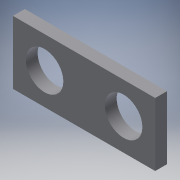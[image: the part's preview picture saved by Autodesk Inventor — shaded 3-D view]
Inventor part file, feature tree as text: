
AUTODESK INVENTOR PART (.ipt)
format: ipt  version: 2016 (Build 200138000, 138)  size: 99,840 bytes
history: native  units: in
note: dims shown in document units (in); Inventor stores cm internally (conversion verified against a paired STEP export)
features: extrude x1, sketch x1, reference x1
ambient origin geometry x8: Origin, YZ Plane, XZ Plane, XY Plane, X Axis, Y Axis, Z Axis, Center Point
bodies: Solid1 (feature_tree)
feature tree (3):
  extrude  "Extrusion1"  Depth=0.0591in
  sketch  "Sketch2"  dims[d0=0.187in d1=0.1575in d2=0.1575in d3=0.9055in d4=0.315in d5=0.0591in d6=0.0in]
  reference  "Reference1"
